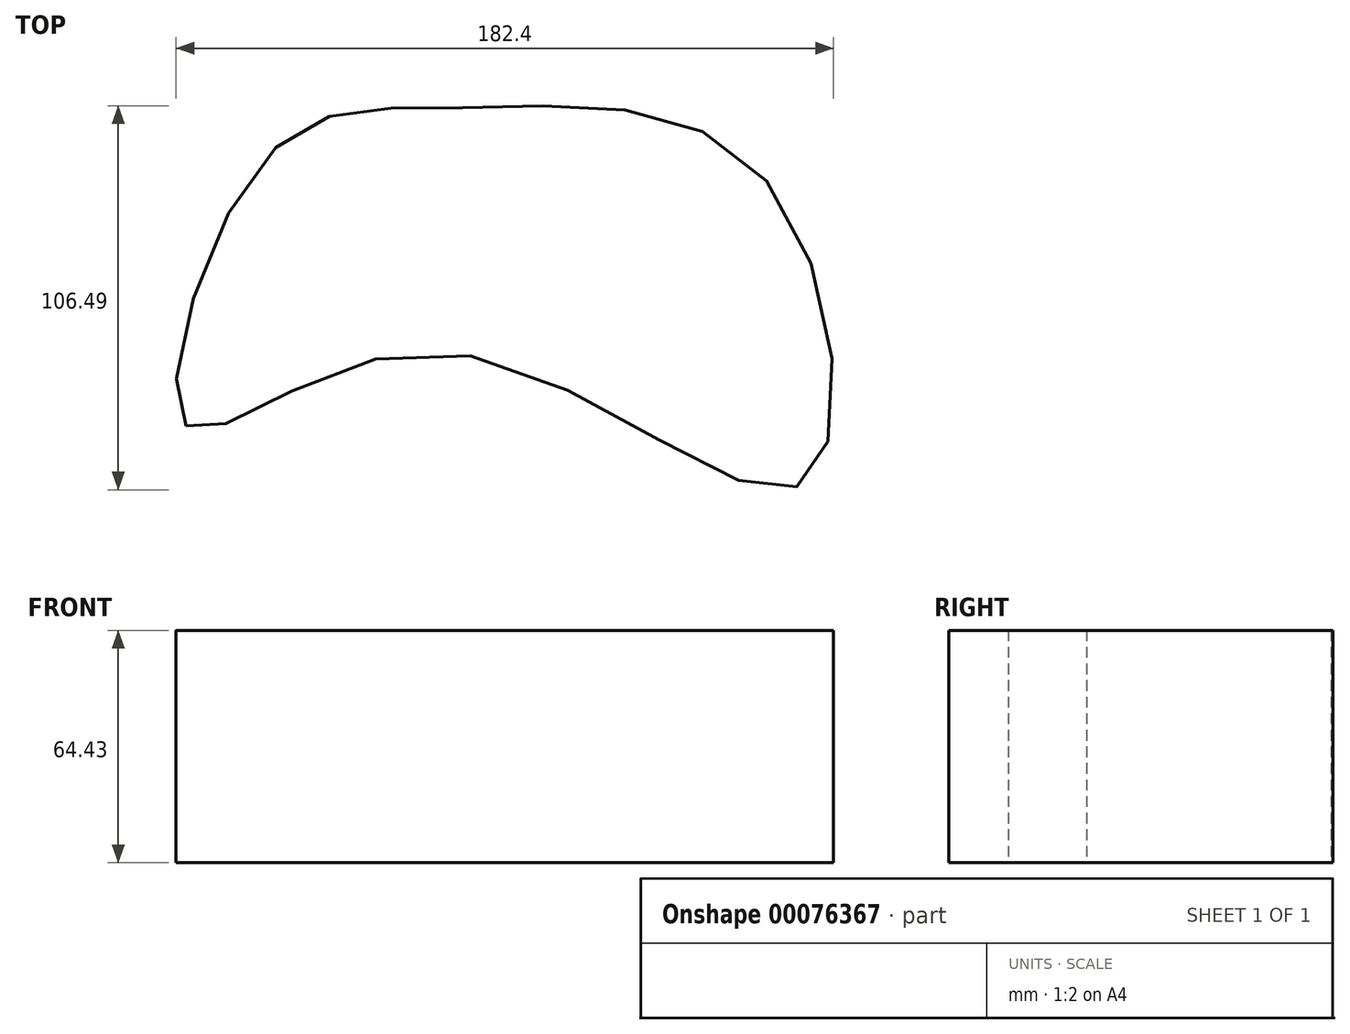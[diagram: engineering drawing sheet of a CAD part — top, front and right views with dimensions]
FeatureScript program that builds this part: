
annotation { "Feature Type Name" : "Feature", "Feature Type Description" : "" }
export const myFeature = defineFeature(function(context is Context, id is Id, definition is map)
    precondition{}
    {
        {
            var Q0;
            Q0=qCreatedBy(makeId("Top.planeOp"),FACE);
            var sketch = newSketch(context, id + "F0", { "sketchPlane" : qUnion([Q0])});
            skFitSpline(sketch, "E0", {"points": [v(-69.17, -29.98) * mm, v(0, -9.45) * mm, v(101.36, -46.32) * mm, v(91.2, 38.88) * mm, v(6.9, 58.32) * mm, v(-47.75, 43.6) * mm, v(-69.17, -29.98) * mm]});
            skSolve(sketch);
        }
        {
            var Q0;
            Q0=makeQuery(id+"F0.imprint","IMPRINT",FACE,{"disambiguationData":[TD([[makeQuery(id+"F0.imprint","IMPRINT",EDGE,{"derivedFrom":sQuery(id+"F0.wireOp",EDGE,"E0")}),1.0]])]});
            extrude(context, id + "F1", {"entities" : qUnion([Q0]), "depth" : 64.43 * mm});
        }
    });
